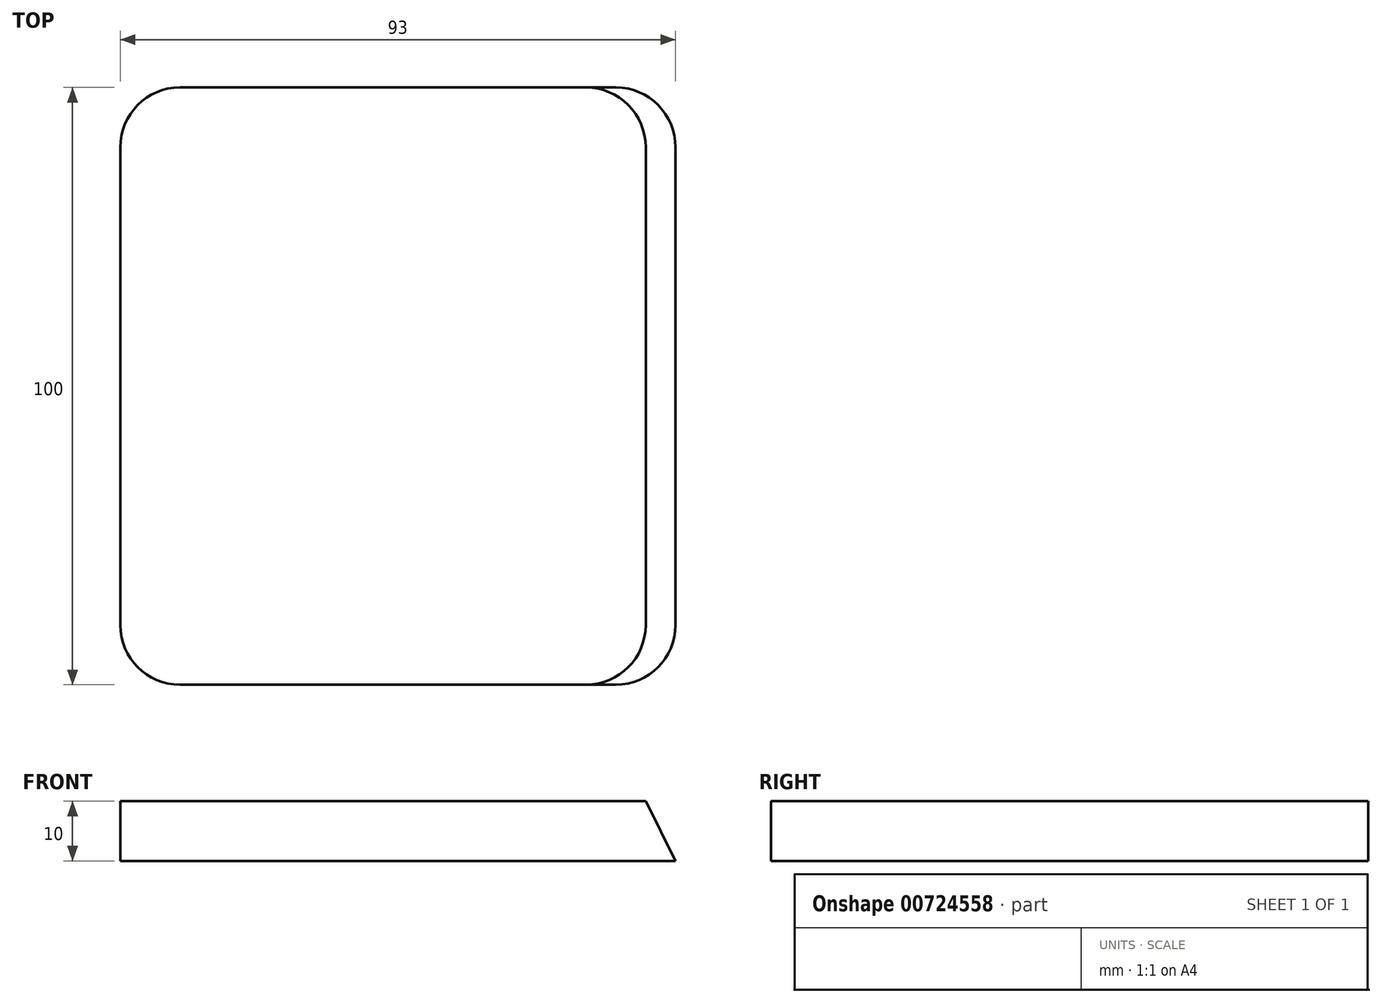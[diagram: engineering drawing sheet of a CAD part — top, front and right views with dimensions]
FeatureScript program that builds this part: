
annotation { "Feature Type Name" : "Feature", "Feature Type Description" : "" }
export const myFeature = defineFeature(function(context is Context, id is Id, definition is map)
    precondition{}
    {
        {
            var Q0;
            Q0=qCreatedBy(makeId("Top.planeOp"),FACE);
            var sketch = newSketch(context, id + "F0", { "sketchPlane" : qUnion([Q0])});
            skLineSegment(sketch, "E0.bottom", {"start": v(10, 50) * mm, "end": v(83, 50) * mm});
            skLineSegment(sketch, "E0.top", {"start": v(10, -50) * mm, "end": v(83, -50) * mm});
            skLineSegment(sketch, "E0.left", {"start": v(0, 40) * mm, "end": v(0, -40) * mm});
            skLineSegment(sketch, "E0.right", {"start": v(93, 40) * mm, "end": v(93, -40) * mm});
            skPoint(sketch, "E1.visualSharp", {"position": v(93, -50) * mm});
            skArc(sketch, "E1.filletArc", {"start": v(83, -50) * mm, "mid": v(90.07, -47.07) * mm, "end": v(93, -40) * mm});
            skPoint(sketch, "E2.visualSharp", {"position": v(93, 50) * mm});
            skArc(sketch, "E2.filletArc", {"start": v(93, 40) * mm, "mid": v(90.07, 47.07) * mm, "end": v(83, 50) * mm});
            skPoint(sketch, "E3.visualSharp", {"position": v(0, 50) * mm});
            skArc(sketch, "E3.filletArc", {"start": v(10, 50) * mm, "mid": v(2.93, 47.07) * mm, "end": v(0, 40) * mm});
            skPoint(sketch, "E4.visualSharp", {"position": v(0, -50) * mm});
            skArc(sketch, "E4.filletArc", {"start": v(0, -40) * mm, "mid": v(2.93, -47.07) * mm, "end": v(10, -50) * mm});
            skSolve(sketch);
        }
        {
            var Q0;
            Q0=qCreatedBy(makeId("Top.planeOp"),FACE);
            cPlane(context, id + "F1", {"entities" : qUnion([Q0]), "cplaneType" : CPlaneType.OFFSET, "offset" : 10 * mm, "width" : 150 * mm, "height" : 150 * mm});
        }
        {
            var Q0;
            Q0=qCreatedBy(id+"F1.planeOp",FACE);
            var sketch = newSketch(context, id + "F2", { "sketchPlane" : qUnion([Q0])});
            skLineSegment(sketch, "E5.bottom", {"start": v(10, 50) * mm, "end": v(78, 50) * mm});
            skLineSegment(sketch, "E5.top", {"start": v(10, -50) * mm, "end": v(78, -50) * mm});
            skLineSegment(sketch, "E5.left", {"start": v(0, 40) * mm, "end": v(0, -40) * mm});
            skLineSegment(sketch, "E5.right", {"start": v(88, 40) * mm, "end": v(88, -40) * mm});
            skPoint(sketch, "E6.visualSharp", {"position": v(88, -50) * mm});
            skArc(sketch, "E6.filletArc", {"start": v(78, -50) * mm, "mid": v(85.07, -47.07) * mm, "end": v(88, -40) * mm});
            skPoint(sketch, "E7.visualSharp", {"position": v(88, 50) * mm});
            skArc(sketch, "E7.filletArc", {"start": v(88, 40) * mm, "mid": v(85.07, 47.07) * mm, "end": v(78, 50) * mm});
            skPoint(sketch, "E8.visualSharp", {"position": v(0, 50) * mm});
            skArc(sketch, "E8.filletArc", {"start": v(10, 50) * mm, "mid": v(2.93, 47.07) * mm, "end": v(0, 40) * mm});
            skPoint(sketch, "E9.visualSharp", {"position": v(0, -50) * mm});
            skArc(sketch, "E9.filletArc", {"start": v(0, -40) * mm, "mid": v(2.93, -47.07) * mm, "end": v(10, -50) * mm});
            skSolve(sketch);
        }
        {
            var Q0;
            Q0=qCreatedBy(id+"F1.planeOp",FACE);
            cPlane(context, id + "F3", {"entities" : qUnion([Q0]), "cplaneType" : CPlaneType.OFFSET, "offset" : 10 * mm, "width" : 150 * mm, "height" : 150 * mm});
        }
        {
            var Q0;
            Q0=qCreatedBy(id+"F3.planeOp",FACE);
            cPlane(context, id + "F4", {"entities" : qUnion([Q0]), "cplaneType" : CPlaneType.OFFSET, "offset" : 10 * mm, "width" : 150 * mm, "height" : 150 * mm});
        }
        {
            var Q0;
            Q0=qCreatedBy(id+"F4.planeOp",FACE);
            cPlane(context, id + "F5", {"entities" : qUnion([Q0]), "cplaneType" : CPlaneType.OFFSET, "offset" : 10 * mm, "width" : 150 * mm, "height" : 150 * mm});
        }
        {
            var Q0;
            Q0=qCreatedBy(id+"F5.planeOp",FACE);
            var sketch = newSketch(context, id + "F6", { "sketchPlane" : qUnion([Q0])});
            skLineSegment(sketch, "E10.bottom", {"start": v(10, 50) * mm, "end": v(63, 50) * mm});
            skLineSegment(sketch, "E10.top", {"start": v(10, -50) * mm, "end": v(63, -50) * mm});
            skLineSegment(sketch, "E10.left", {"start": v(0, 40) * mm, "end": v(0, -40) * mm});
            skLineSegment(sketch, "E10.right", {"start": v(73, 40) * mm, "end": v(73, -40) * mm});
            skPoint(sketch, "E11.visualSharp", {"position": v(73, -50) * mm});
            skArc(sketch, "E11.filletArc", {"start": v(63, -50) * mm, "mid": v(70.07, -47.07) * mm, "end": v(73, -40) * mm});
            skPoint(sketch, "E12.visualSharp", {"position": v(73, 50) * mm});
            skArc(sketch, "E12.filletArc", {"start": v(73, 40) * mm, "mid": v(70.07, 47.07) * mm, "end": v(63, 50) * mm});
            skPoint(sketch, "E13.visualSharp", {"position": v(0, 50) * mm});
            skArc(sketch, "E13.filletArc", {"start": v(10, 50) * mm, "mid": v(2.93, 47.07) * mm, "end": v(0, 40) * mm});
            skPoint(sketch, "E14.visualSharp", {"position": v(0, -50) * mm});
            skArc(sketch, "E14.filletArc", {"start": v(0, -40) * mm, "mid": v(2.93, -47.07) * mm, "end": v(10, -50) * mm});
            skArc(sketch, "E15.0", {"start": v(4, -40) * mm, "mid": v(5.76, -44.24) * mm, "end": v(10, -46) * mm});
            skLineSegment(sketch, "E15.1", {"start": v(4, 40) * mm, "end": v(4, -40) * mm});
            skLineSegment(sketch, "E15.2", {"start": v(10, -46) * mm, "end": v(63, -46) * mm});
            skArc(sketch, "E15.3", {"start": v(10, 46) * mm, "mid": v(5.76, 44.24) * mm, "end": v(4, 40) * mm});
            skArc(sketch, "E15.4", {"start": v(63, -46) * mm, "mid": v(67.24, -44.24) * mm, "end": v(69, -40) * mm});
            skLineSegment(sketch, "E15.5", {"start": v(69, 40) * mm, "end": v(69, -40) * mm});
            skArc(sketch, "E15.6", {"start": v(69, 40) * mm, "mid": v(67.24, 44.24) * mm, "end": v(63, 46) * mm});
            skLineSegment(sketch, "E15.7", {"start": v(10, 46) * mm, "end": v(63, 46) * mm});
            skSolve(sketch);
        }
        {
            var Q0;
            Q0=sQuery(id+"F6.wireOp",VERTEX,"E14.visualSharp");
            var Q1;
            Q1=sQuery(id+"F6.wireOp",EDGE,"E10.left");
            cPlane(context, id + "F7", {"entities" : qUnion([Q0, Q1]), "cplaneType" : CPlaneType.LINE_POINT, "offset" : 25 * mm, "width" : 150 * mm, "height" : 150 * mm});
        }
        {
            var Q0;
            Q0=makeQuery(id+"F0.imprint","IMPRINT",FACE,{"disambiguationData":[TD([[makeQuery(id+"F0.imprint","IMPRINT",EDGE,{"derivedFrom":sQuery(id+"F0.wireOp",EDGE,"E0.bottom")}),-1.0]])]});
            var Q1;
            Q1=makeQuery(id+"F2.imprint","IMPRINT",FACE,{"disambiguationData":[TD([[makeQuery(id+"F2.imprint","IMPRINT",EDGE,{"derivedFrom":sQuery(id+"F2.wireOp",EDGE,"E5.bottom")}),-1.0]])]});
            loft(context, id + "F8", {"sheetProfilesArray" : [{ "sheetProfileEntities" : qUnion([Q0]) }, { "sheetProfileEntities" : qUnion([Q1]) }]});
        }
    });
